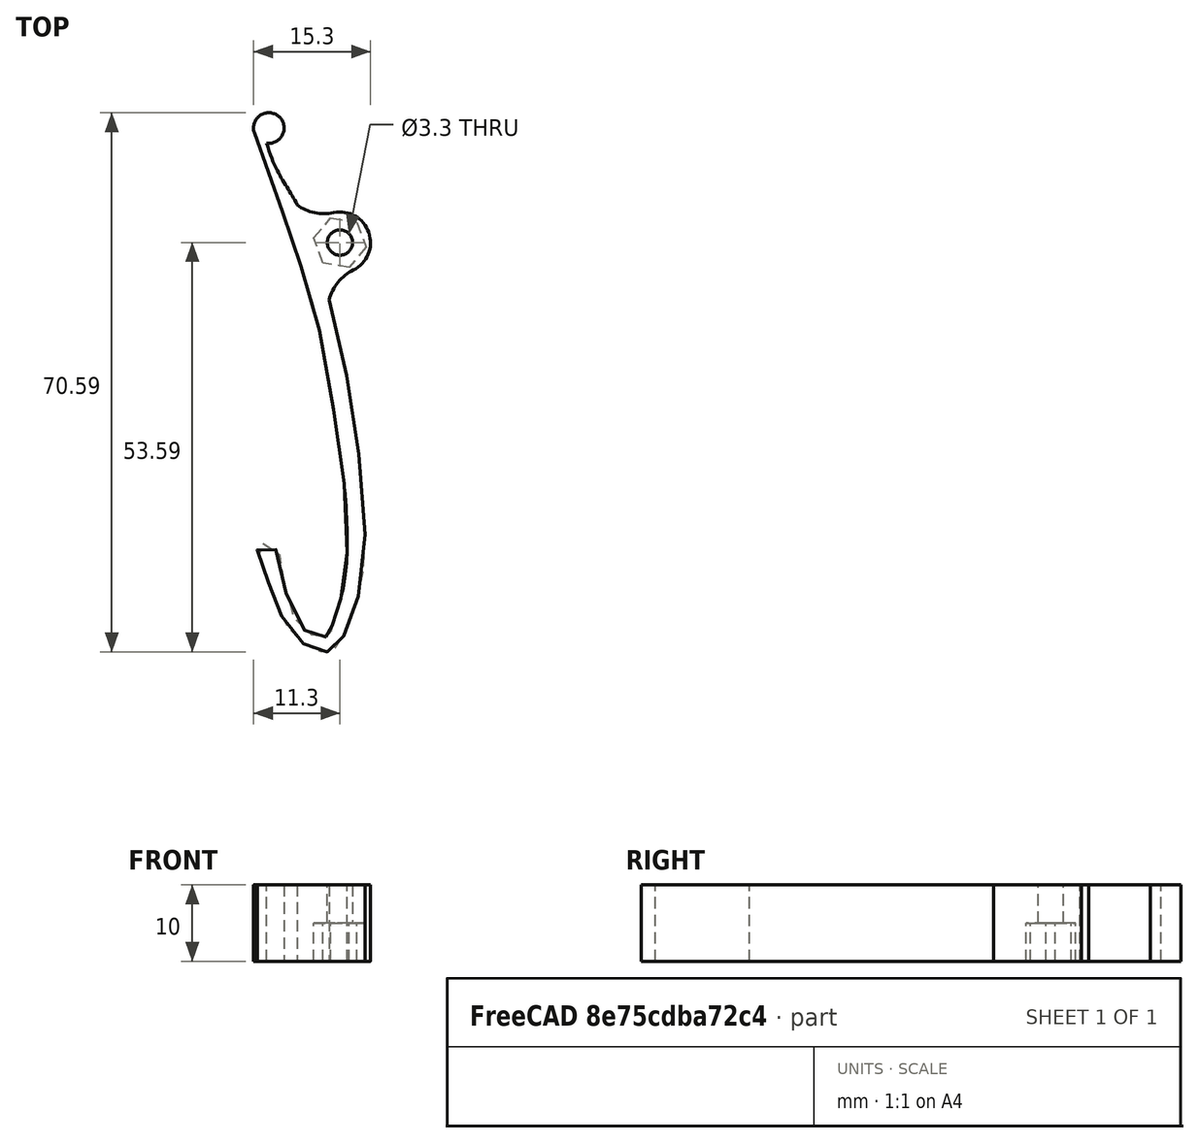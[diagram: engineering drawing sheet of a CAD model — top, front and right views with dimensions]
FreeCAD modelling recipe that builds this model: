
FCSTD DOCUMENT  (FreeCAD 0.20R29603 (Git))
Label: v0.3_RC1_bez_kabla
License: All rights reserved
LicenseURL: http://en.wikipedia.org/wiki/All_rights_reserved
objects: Sketcher::SketchObject×3, PartDesign::Pad×2, PartDesign::Pocket×1, PartDesign::Body×1
note: 10 computed .brp shape members not serialized (recipe doc carries the construction recipe); baked Part::Feature solids carry a one-line shape summary decoded from their .brp

FEATURE [Sketcher::SketchObject] Sketch
  FullyConstrained = false
  MapMode = 5
  Support = -> [XY_Plane]
  sketch-geometry (34):
    g0: ArcOfCircle CenterX=0 CenterY=50 CenterZ=0 NormalX=0 NormalY=0 NormalZ=1 AngleXU=0 Radius=2 StartAngle=4.57657 EndAngle=9.72822
    g1: LineSegment StartX=0 StartY=0 StartZ=0 EndX=0 EndY=-10 EndZ=0
    g2-g30: Circle x29 (B-spline internal-alignment scaffolding for g31; pole/knot coordinates omitted)
    g31: BSplineCurve PolesCount=29 KnotsCount=27 Degree=3 IsPeriodic=0
    g32: GeomPoint X=-1.90863 Y=49.4024 Z=0
    g33: Circle CenterX=0 CenterY=-6.51 CenterZ=0 NormalX=0 NormalY=0 NormalZ=1 AngleXU=0 Radius=1.43333
  constraints (14):
    c: PointOnObject(g0,g-2)
    c: Diameter(g0) = 4
    c: DistanceY(g-1,g0) = 50
    c: Coincident(g1,g-1)
    c: PointOnObject(g1,g-2)
    c: DistanceY(g1,g1) = 10
    c: Weight(g2) = 1
    c: Equal(g2, g3-g30) x28
    c: InternalAlignment(g2-g30 -> g31) x29
    c: InternalAlignment(g32,g31)
    c: DistanceX(g33) = 0
    c: DistanceY(g33) = -6.51
    c: Coincident(g31,g0)
    c: Coincident(g0,g31)
FEATURE [PartDesign::Pad] Pad
  Direction = (0,0,1)
  Length = 10
  Length2 = 10
  Profile = -> Sketch
  ReferenceAxis = -> Sketch [N_Axis]
  Type = 0
FEATURE [Sketcher::SketchObject] Sketch001
  FullyConstrained = true
  MapMode = 5
  Placement = pos=(0,0,10) rot=(0,0,1;0rad)
  Support = -> [Pad]
  sketch-geometry (7):
    g0: ArcOfCircle CenterX=9.3 CenterY=35 CenterZ=0 NormalX=0 NormalY=0 NormalZ=1 AngleXU=0 Radius=4 StartAngle=5.16832 EndAngle=8.06128
    g1: LineSegment StartX=3.23895 StartY=40.3164 StartZ=0 EndX=7.7969 EndY=27.0791 EndZ=0
    g2: GeomPoint X=5.51793 Y=33.6977 Z=0
    g3: ArcOfCircle CenterX=7.24184 CenterY=44.7859 CenterZ=0 NormalX=0 NormalY=0 NormalZ=1 AngleXU=0 Radius=6 StartAngle=3.98201 EndAngle=4.91969
    g4: ArcOfCircle CenterX=13.703 CenterY=26.0215 CenterZ=0 NormalX=0 NormalY=0 NormalZ=1 AngleXU=0 Radius=6 StartAngle=2.02672 EndAngle=2.9644
    g5: Circle CenterX=9.3 CenterY=35 CenterZ=0 NormalX=0 NormalY=0 NormalZ=1 AngleXU=0 Radius=1.65
    g6: LineSegment StartX=8.47674 StartY=38.9144 StartZ=0 EndX=11.0612 EndY=31.4086 EndZ=0
  constraints (18):
    c: Diameter(g0) = 8
    c: DistanceX(g0) = 9.3
    c: DistanceY(g0) = 35
    c: Distance(g1) = 14
    c: Symmetric(g1,g1,g2)
    c: PointOnObject(g2,g0)
    c: Coincident(g3,g1)
    c: Coincident(g4,g1)
    c: Radius(g3) = 6
    c: Radius(g4) = 6
    c: Coincident(g5,g0)
    c: Diameter(g5) = 3.3
    c: Angle(g1,g-1) = 1.23918
    c: Tangent(g0,g3) = 1.5708
    c: Tangent(g0,g4) = 1.5708
    c: Coincident(g6,g0)
    c: Coincident(g6,g0)
    c: Parallel(g6,g1)
FEATURE [PartDesign::Pad] Pad001
  BaseFeature = -> Pad
  Direction = (0,0,1)
  Length = 10
  Length2 = 10
  Profile = -> Sketch001
  ReferenceAxis = -> Sketch001 [N_Axis]
  Reversed = true
  Type = 0
FEATURE [Sketcher::SketchObject] Sketch002
  FullyConstrained = false
  MapMode = 5
  Placement = pos=(0,0,-1.8e-15) rot=(1,0,0;3.14159rad)
  Support = -> [Pad001]
  sketch-geometry (7):
    g0: LineSegment StartX=8.11724 StartY=-38.2559 StartZ=0 EndX=11.5283 EndY=-37.6523 EndZ=0
    g1: LineSegment StartX=11.5283 StartY=-37.6523 StartZ=0 EndX=12.7111 EndY=-34.3963 EndZ=0
    g2: LineSegment StartX=12.7111 StartY=-34.3963 StartZ=0 EndX=10.4828 EndY=-31.7441 EndZ=0
    g3: LineSegment StartX=10.4828 StartY=-31.7441 StartZ=0 EndX=7.07166 EndY=-32.3477 EndZ=0
    g4: LineSegment StartX=7.07166 StartY=-32.3477 StartZ=0 EndX=5.8889 EndY=-35.6037 EndZ=0
    g5: LineSegment StartX=5.8889 StartY=-35.6037 StartZ=0 EndX=8.11724 EndY=-38.2559 EndZ=0
    g6: Circle CenterX=9.3 CenterY=-35 CenterZ=0 NormalX=0 NormalY=0 NormalZ=1 AngleXU=0 Radius=3.4641
  constraints (16):
    c: Coincident(g0,g1)
    c: Coincident(g1,g2)
    c: Coincident(g2,g3)
    c: Coincident(g3,g4)
    c: Coincident(g4,g5)
    c: Coincident(g5,g0)
    c: Equal(g0, g1-g5) x5
    c: PointOnObject(g0,g6)
    c: PointOnObject(g1,g6)
    c: PointOnObject(g2,g6)
    c: PointOnObject(g3,g6)
    c: PointOnObject(g4,g6)
    c: PointOnObject(g5,g6)
    c: Distance(g4,g0) = 6
    c: DistanceX(g6) = 9.3
    c: DistanceY(g6) = -35
FEATURE [PartDesign::Pocket] Pocket
  BaseFeature = -> Pad001
  Direction = (0,0,1)
  Length = 5
  Length2 = 5
  Profile = -> Sketch002
  ReferenceAxis = -> Sketch002 [N_Axis]
  Type = 0
FEATURE [PartDesign::Body] Body
  Group = -> [Sketch,Pad,Sketch001,Pad001,Sketch002,Pocket]
  Origin = -> Origin
  Tip = -> Pocket
